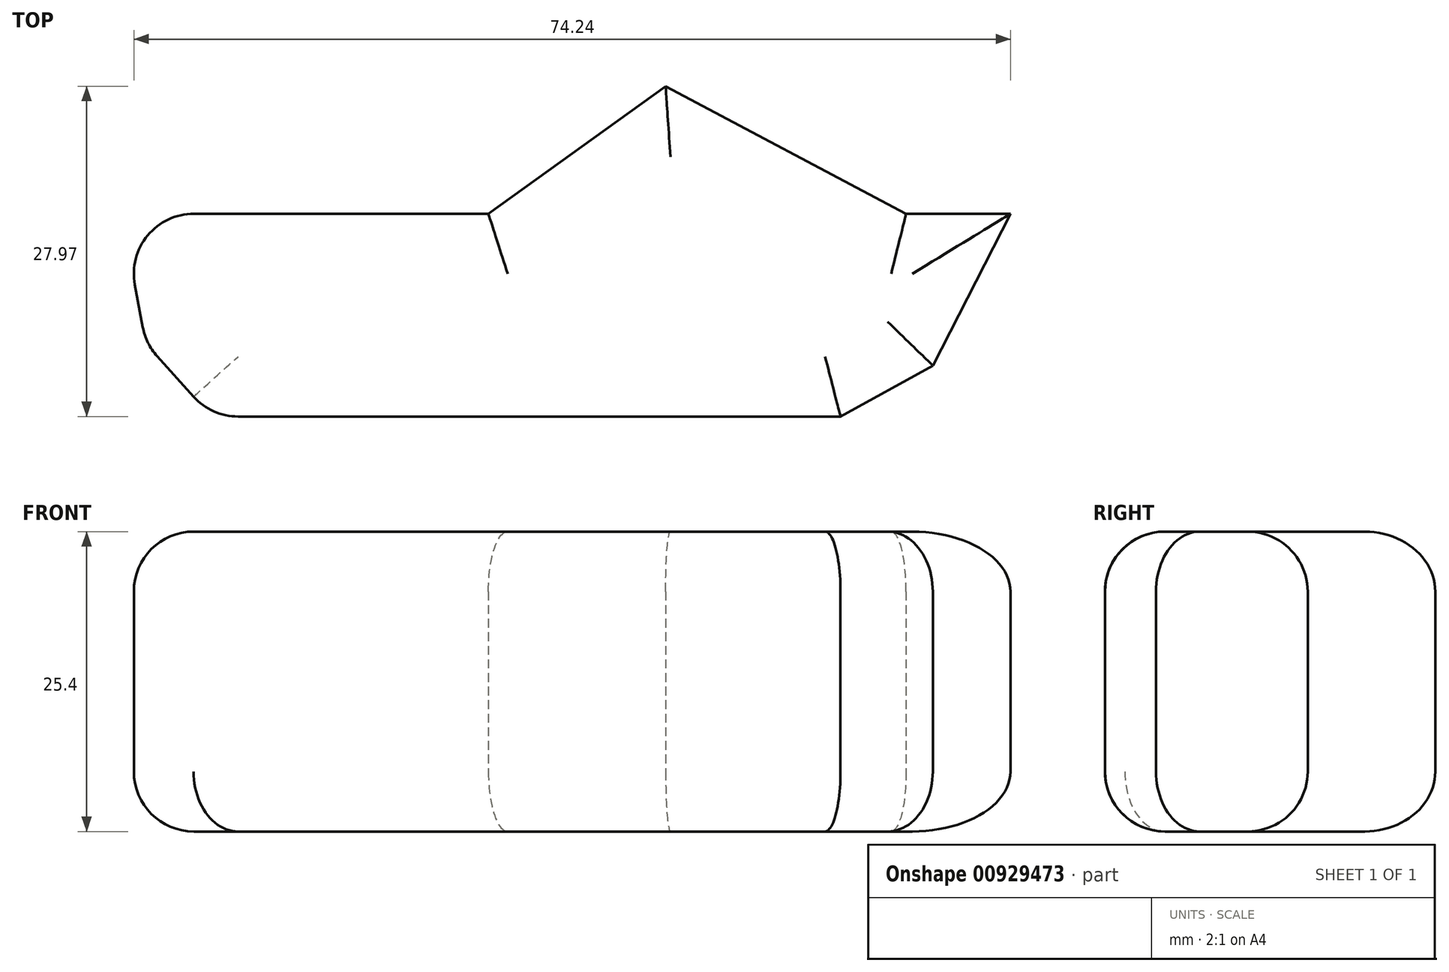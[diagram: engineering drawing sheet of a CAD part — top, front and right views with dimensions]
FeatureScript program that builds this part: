
annotation { "Feature Type Name" : "Feature", "Feature Type Description" : "" }
export const myFeature = defineFeature(function(context is Context, id is Id, definition is map)
    precondition{}
    {
        {
            var Q0;
            Q0=qCreatedBy(makeId("Top.planeOp"),FACE);
            var sketch = newSketch(context, id + "F0", { "sketchPlane" : qUnion([Q0])});
            skLineSegment(sketch, "E0.bottom", {"start": v(-37.64, -21.9) * mm, "end": v(37.64, -21.9) * mm});
            skLineSegment(sketch, "E0.top", {"start": v(-37.64, 21.9) * mm, "end": v(37.64, 21.9) * mm});
            skLineSegment(sketch, "E0.left", {"start": v(-37.64, -21.9) * mm, "end": v(-37.64, 21.9) * mm});
            skLineSegment(sketch, "E0.right", {"start": v(37.64, -21.9) * mm, "end": v(37.64, 21.9) * mm});
            skPoint(sketch, "E0.middle", {"position": v(0, 0) * mm});
            skLineSegment(sketch, "E1", {"start": v(-37.64, 0) * mm, "end": v(-6.58, 0) * mm});
            skLineSegment(sketch, "E2", {"start": v(-6.58, 0) * mm, "end": v(8.43, 10.8) * mm});
            skLineSegment(sketch, "E3", {"start": v(8.43, 10.8) * mm, "end": v(28.8, 0) * mm});
            skLineSegment(sketch, "E4", {"start": v(28.8, 0) * mm, "end": v(41.14, 0) * mm});
            skPoint(sketch, "E4.endSnap0", {"position": v(37.64, 0) * mm});
            skLineSegment(sketch, "E5", {"start": v(37.64, 0) * mm, "end": v(31.06, -12.86) * mm});
            skLineSegment(sketch, "E6", {"start": v(31.06, -12.86) * mm, "end": v(23.24, -17.17) * mm});
            skLineSegment(sketch, "E7", {"start": v(23.24, -17.17) * mm, "end": v(-30.03, -17.17) * mm});
            skLineSegment(sketch, "E8", {"start": v(-30.03, -17.17) * mm, "end": v(-35.58, -11) * mm});
            skLineSegment(sketch, "E9", {"start": v(-35.58, -11) * mm, "end": v(-37.64, 0) * mm});
            skSolve(sketch);
        }
        {
            var Q0;
            Q0=makeQuery(id+"F0.imprint","IMPRINT",FACE,{"disambiguationData":[TD([[makeQuery(id+"F0.imprint","IMPRINT",EDGE,{"derivedFrom":sQuery(id+"F0.wireOp",EDGE,"E1")}),-1.0]])]});
            var sketch = newSketch(context, id + "F1", { "sketchPlane" : qUnion([Q0])});
            skSolve(sketch);
        }
        {
            var Q0;
            Q0=makeQuery(id+"F1.imprint","IMPRINT",FACE,{"disambiguationData":[TD([[makeQuery(id+"F1.imprint","IMPRINT",EDGE,{"derivedFrom":makeQuery(id+"F0.imprint","IMPRINT",EDGE,{"derivedFrom":sQuery(id+"F0.wireOp",EDGE,"E1")})}),-1.0]])]});
            extrude(context, id + "F2", {"entities" : qUnion([Q0]), "depth" : 25.4 * mm, "offsetDistance" : 25.4 * mm});
        }
        {
            var Q0;
            Q0=makeQuery(id+"F2.opExtrude","CAP_EDGE",EDGE,{"disambiguationData":[OSD([sQuery(id+"F0.wireOp",EDGE,"E1")])],"isStart":false});
            var Q1;
            Q1=makeQuery(id+"F2.opExtrude","CAP_EDGE",EDGE,{"disambiguationData":[OSD([sQuery(id+"F0.wireOp",EDGE,"E3")])],"isStart":false});
            var Q2;
            Q2=makeQuery(id+"F2.opExtrude","CAP_EDGE",EDGE,{"disambiguationData":[OSD([sQuery(id+"F0.wireOp",EDGE,"E4")])],"isStart":false});
            var Q3;
            Q3=makeQuery(id+"F2.opExtrude","CAP_EDGE",EDGE,{"disambiguationData":[OSD([sQuery(id+"F0.wireOp",EDGE,"E5")])],"isStart":false});
            var Q4;
            Q4=makeQuery(id+"F2.opExtrude","CAP_EDGE",EDGE,{"disambiguationData":[OSD([sQuery(id+"F0.wireOp",EDGE,"E6")])],"isStart":false});
            var Q5;
            Q5=makeQuery(id+"F2.opExtrude","CAP_EDGE",EDGE,{"disambiguationData":[OSD([sQuery(id+"F0.wireOp",EDGE,"E7")])],"isStart":false});
            var Q6;
            Q6=makeQuery(id+"F2.opExtrude","CAP_EDGE",EDGE,{"disambiguationData":[OSD([sQuery(id+"F0.wireOp",EDGE,"E8")])],"isStart":false});
            var Q7;
            Q7=makeQuery(id+"F2.opExtrude","CAP_EDGE",EDGE,{"disambiguationData":[OSD([sQuery(id+"F0.wireOp",EDGE,"E9")])],"isStart":false});
            var Q8;
            Q8=makeQuery(id+"F2.opExtrude","CAP_EDGE",EDGE,{"disambiguationData":[OSD([sQuery(id+"F0.wireOp",EDGE,"E8")])],"isStart":true});
            var Q9;
            Q9=makeQuery(id+"F2.opExtrude","CAP_EDGE",EDGE,{"disambiguationData":[OSD([sQuery(id+"F0.wireOp",EDGE,"E9")])],"isStart":true});
            var Q10;
            Q10=makeQuery(id+"F2.opExtrude","SWEPT_EDGE",EDGE,{"disambiguationData":[OSD([sQuery(id+"F0.wireOp",EDGE,"E8"),sQuery(id+"F0.wireOp",EDGE,"E9")])]});
            var Q11;
            Q11=makeQuery(id+"F2.opExtrude","CAP_FACE",FACE,{"disambiguationData":[OSD([sQuery(id+"F0.wireOp",EDGE,"E1"),sQuery(id+"F0.wireOp",EDGE,"E2"),sQuery(id+"F0.wireOp",EDGE,"E3"),sQuery(id+"F0.wireOp",EDGE,"E4"),sQuery(id+"F0.wireOp",EDGE,"E5"),sQuery(id+"F0.wireOp",EDGE,"E6"),sQuery(id+"F0.wireOp",EDGE,"E7"),sQuery(id+"F0.wireOp",EDGE,"E8"),sQuery(id+"F0.wireOp",EDGE,"E9")])],"isStart":false});
            fillet(context, id + "F3", {"entities" : qUnion([Q0, Q1, Q2, Q3, Q4, Q5, Q6, Q7, Q8, Q9, Q10, Q11]), "radius" : 5.08 * mm, "tangentPropagation" : true, "allowEdgeOverflow" : false});
        }
        {
            var Q0;
            {var subQ0=sQuery(id+"F0.wireOp",EDGE,"E2");Q0=makeQuery(id+"F3.opFillet","BLEND_EDGE",EDGE,{"blendedFrom":[makeQuery(id+"F2.opExtrude","CAP_EDGE",EDGE,{"disambiguationData":[OSD([subQ0])],"isStart":false}),makeQuery(id+"F2.opExtrude","CAP_FACE",FACE,{"disambiguationData":[OSD([sQuery(id+"F0.wireOp",EDGE,"E1"),subQ0,sQuery(id+"F0.wireOp",EDGE,"E3"),sQuery(id+"F0.wireOp",EDGE,"E4"),sQuery(id+"F0.wireOp",EDGE,"E5"),sQuery(id+"F0.wireOp",EDGE,"E6"),sQuery(id+"F0.wireOp",EDGE,"E7"),sQuery(id+"F0.wireOp",EDGE,"E8"),sQuery(id+"F0.wireOp",EDGE,"E9")])],"isStart":false})],"blendedInto":[makeQuery(id+"F2.opExtrude","CAP_FACE",FACE,{"disambiguationData":[OSD([sQuery(id+"F0.wireOp",EDGE,"E1"),subQ0,sQuery(id+"F0.wireOp",EDGE,"E3"),sQuery(id+"F0.wireOp",EDGE,"E4"),sQuery(id+"F0.wireOp",EDGE,"E5"),sQuery(id+"F0.wireOp",EDGE,"E6"),sQuery(id+"F0.wireOp",EDGE,"E7"),sQuery(id+"F0.wireOp",EDGE,"E8"),sQuery(id+"F0.wireOp",EDGE,"E9")])],"isStart":false})]});}
            var Q1;
            Q1=makeQuery(id+"F2.opExtrude","CAP_EDGE",EDGE,{"disambiguationData":[OSD([sQuery(id+"F0.wireOp",EDGE,"E7")])],"isStart":true});
            var Q2;
            {var subQ0=sQuery(id+"F0.wireOp",EDGE,"E9");Q2=makeQuery(id+"F3.opFillet","BLEND_EDGE",EDGE,{"blendedFrom":[makeQuery(id+"F2.opExtrude","CAP_EDGE",EDGE,{"disambiguationData":[OSD([subQ0])],"isStart":true}),makeQuery(id+"F2.opExtrude","CAP_FACE",FACE,{"disambiguationData":[OSD([sQuery(id+"F0.wireOp",EDGE,"E1"),sQuery(id+"F0.wireOp",EDGE,"E2"),sQuery(id+"F0.wireOp",EDGE,"E3"),sQuery(id+"F0.wireOp",EDGE,"E4"),sQuery(id+"F0.wireOp",EDGE,"E5"),sQuery(id+"F0.wireOp",EDGE,"E6"),sQuery(id+"F0.wireOp",EDGE,"E7"),sQuery(id+"F0.wireOp",EDGE,"E8"),subQ0])],"isStart":true})],"blendedInto":[makeQuery(id+"F2.opExtrude","CAP_FACE",FACE,{"disambiguationData":[OSD([sQuery(id+"F0.wireOp",EDGE,"E1"),sQuery(id+"F0.wireOp",EDGE,"E2"),sQuery(id+"F0.wireOp",EDGE,"E3"),sQuery(id+"F0.wireOp",EDGE,"E4"),sQuery(id+"F0.wireOp",EDGE,"E5"),sQuery(id+"F0.wireOp",EDGE,"E6"),sQuery(id+"F0.wireOp",EDGE,"E7"),sQuery(id+"F0.wireOp",EDGE,"E8"),subQ0])],"isStart":true})]});}
            var Q3;
            Q3=makeQuery(id+"F2.opExtrude","CAP_EDGE",EDGE,{"disambiguationData":[OSD([sQuery(id+"F0.wireOp",EDGE,"E1")])],"isStart":true});
            var Q4;
            Q4=makeQuery(id+"F2.opExtrude","CAP_EDGE",EDGE,{"disambiguationData":[OSD([sQuery(id+"F0.wireOp",EDGE,"E2")])],"isStart":true});
            var Q5;
            Q5=makeQuery(id+"F2.opExtrude","CAP_EDGE",EDGE,{"disambiguationData":[OSD([sQuery(id+"F0.wireOp",EDGE,"E3")])],"isStart":true});
            var Q6;
            Q6=makeQuery(id+"F2.opExtrude","CAP_EDGE",EDGE,{"disambiguationData":[OSD([sQuery(id+"F0.wireOp",EDGE,"E4")])],"isStart":true});
            var Q7;
            Q7=makeQuery(id+"F2.opExtrude","CAP_EDGE",EDGE,{"disambiguationData":[OSD([sQuery(id+"F0.wireOp",EDGE,"E6")])],"isStart":true});
            var Q8;
            {var subQ0=sQuery(id+"F0.wireOp",EDGE,"E8");Q8=makeQuery(id+"F3.opFillet","BLEND_EDGE",EDGE,{"blendedFrom":[makeQuery(id+"F2.opExtrude","CAP_EDGE",EDGE,{"disambiguationData":[OSD([subQ0])],"isStart":true}),makeQuery(id+"F2.opExtrude","CAP_FACE",FACE,{"disambiguationData":[OSD([sQuery(id+"F0.wireOp",EDGE,"E1"),sQuery(id+"F0.wireOp",EDGE,"E2"),sQuery(id+"F0.wireOp",EDGE,"E3"),sQuery(id+"F0.wireOp",EDGE,"E4"),sQuery(id+"F0.wireOp",EDGE,"E5"),sQuery(id+"F0.wireOp",EDGE,"E6"),sQuery(id+"F0.wireOp",EDGE,"E7"),subQ0,sQuery(id+"F0.wireOp",EDGE,"E9")])],"isStart":true})],"blendedInto":[makeQuery(id+"F2.opExtrude","CAP_FACE",FACE,{"disambiguationData":[OSD([sQuery(id+"F0.wireOp",EDGE,"E1"),sQuery(id+"F0.wireOp",EDGE,"E2"),sQuery(id+"F0.wireOp",EDGE,"E3"),sQuery(id+"F0.wireOp",EDGE,"E4"),sQuery(id+"F0.wireOp",EDGE,"E5"),sQuery(id+"F0.wireOp",EDGE,"E6"),sQuery(id+"F0.wireOp",EDGE,"E7"),subQ0,sQuery(id+"F0.wireOp",EDGE,"E9")])],"isStart":true})]});}
            var Q9;
            Q9=makeQuery(id+"F2.opExtrude","CAP_FACE",FACE,{"disambiguationData":[OSD([sQuery(id+"F0.wireOp",EDGE,"E1"),sQuery(id+"F0.wireOp",EDGE,"E2"),sQuery(id+"F0.wireOp",EDGE,"E3"),sQuery(id+"F0.wireOp",EDGE,"E4"),sQuery(id+"F0.wireOp",EDGE,"E5"),sQuery(id+"F0.wireOp",EDGE,"E6"),sQuery(id+"F0.wireOp",EDGE,"E7"),sQuery(id+"F0.wireOp",EDGE,"E8"),sQuery(id+"F0.wireOp",EDGE,"E9")])],"isStart":true});
            fillet(context, id + "F4", {"entities" : qUnion([Q0, Q1, Q2, Q3, Q4, Q5, Q6, Q7, Q8, Q9]), "radius" : 5.08 * mm, "tangentPropagation" : true, "allowEdgeOverflow" : false});
        }
    });
